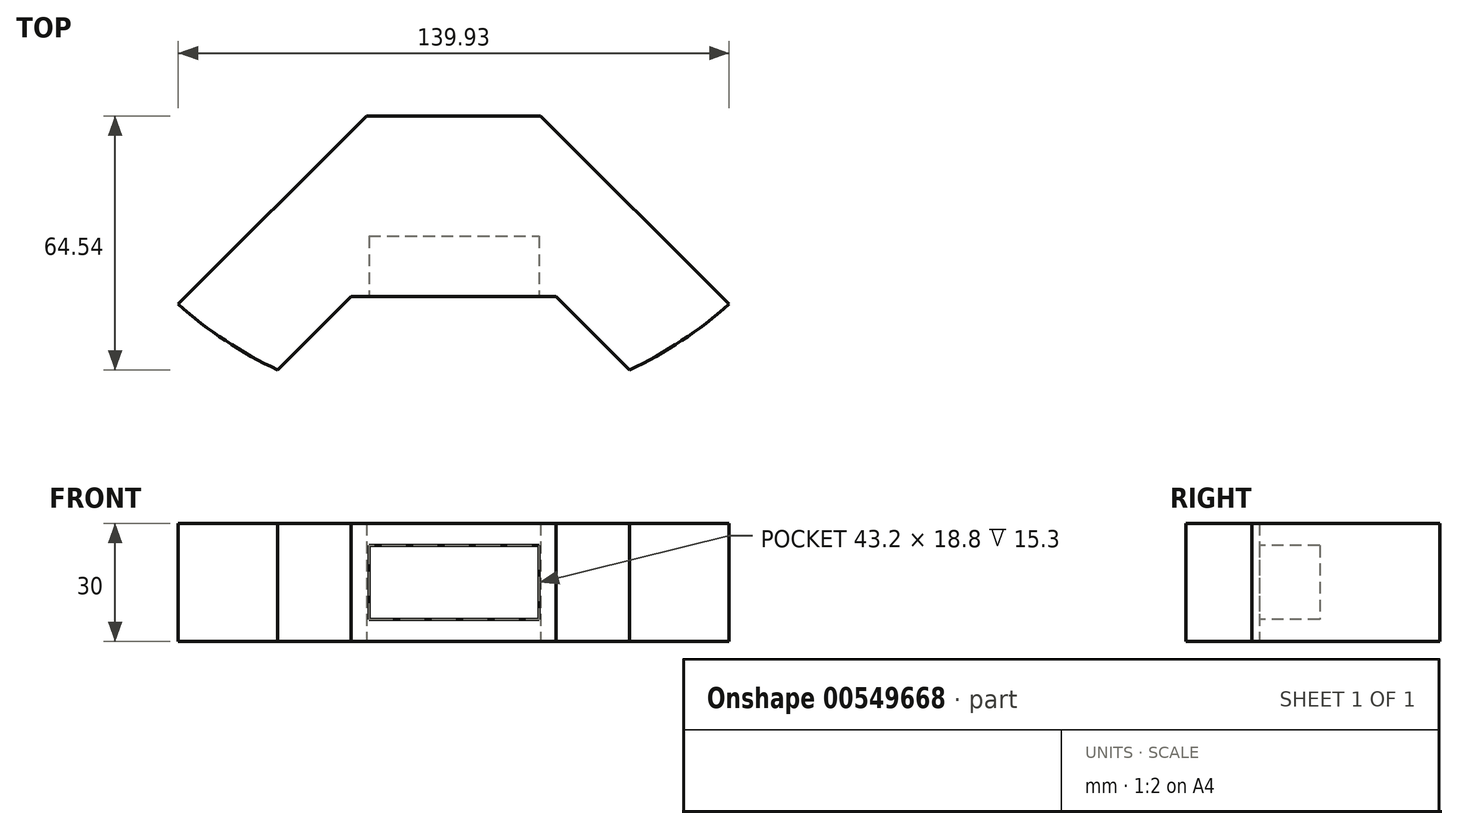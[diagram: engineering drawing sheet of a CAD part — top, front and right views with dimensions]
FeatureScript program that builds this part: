
annotation { "Feature Type Name" : "Feature", "Feature Type Description" : "" }
export const myFeature = defineFeature(function(context is Context, id is Id, definition is map)
    precondition{}
    {
        {
            var Q0;
            Q0=qCreatedBy(makeId("Top.planeOp"),FACE);
            var sketch = newSketch(context, id + "F0", { "sketchPlane" : qUnion([Q0])});
            skCircle(sketch, "E0", {"center": v(-0.1, 1.02) * mm, "radius": 105 * mm});
            skLineSegment(sketch, "E1", {"start": v(-0.1, 106.02) * mm, "end": v(-0.1, -103.98) * mm});
            skLineSegment(sketch, "E2", {"start": v(-0.1, 1.02) * mm, "end": v(-74.34, -73.22) * mm});
            skLineSegment(sketch, "E3", {"start": v(-0.1, 1.02) * mm, "end": v(74.15, -73.22) * mm});
            skLineSegment(sketch, "E4", {"start": v(-0.1, 1.02) * mm, "end": v(-0.1, 106.02) * mm});
            skLineSegment(sketch, "E5", {"start": v(-0.1, -49.26) * mm, "end": v(-44.81, -93.98) * mm});
            skLineSegment(sketch, "E6", {"start": v(-0.1, -49.26) * mm, "end": v(44.63, -93.98) * mm});
            skLineSegment(sketch, "E7", {"start": v(-18.48, 104.81) * mm, "end": v(-0.08, 104.81) * mm});
            skLineSegment(sketch, "E8.bottom", {"start": v(-18.48, 104.81) * mm, "end": v(18.7, 104.81) * mm});
            skLineSegment(sketch, "E8.top", {"start": v(-18.48, 26.11) * mm, "end": v(18.7, 26.11) * mm});
            skLineSegment(sketch, "E8.left", {"start": v(-18.48, 104.81) * mm, "end": v(-18.48, 26.11) * mm});
            skLineSegment(sketch, "E8.right", {"start": v(18.7, 104.81) * mm, "end": v(18.7, 26.11) * mm});
            skLineSegment(sketch, "E9.bottom", {"start": v(-39.87, 13.1) * mm, "end": v(-13.5, -13.1) * mm});
            skLineSegment(sketch, "E9.top", {"start": v(-95.34, -42.72) * mm, "end": v(-68.97, -68.93) * mm});
            skLineSegment(sketch, "E9.left", {"start": v(-39.87, 13.1) * mm, "end": v(-95.34, -42.72) * mm});
            skLineSegment(sketch, "E9.right", {"start": v(-13.5, -13.1) * mm, "end": v(-68.97, -68.93) * mm});
            skLineSegment(sketch, "E10.bottom", {"start": v(14.2, -12.89) * mm, "end": v(40.59, 13.3) * mm});
            skLineSegment(sketch, "E10.top", {"start": v(69.66, -68.73) * mm, "end": v(96.04, -42.54) * mm});
            skLineSegment(sketch, "E10.left", {"start": v(14.2, -12.89) * mm, "end": v(69.66, -68.73) * mm});
            skLineSegment(sketch, "E10.right", {"start": v(40.59, 13.3) * mm, "end": v(96.04, -42.54) * mm});
            skLineSegment(sketch, "E11.bottom", {"start": v(-53.06, 61.6) * mm, "end": v(-40.34, 61.6) * mm});
            skLineSegment(sketch, "E11.top", {"start": v(-53.06, 42.87) * mm, "end": v(-40.34, 42.87) * mm});
            skLineSegment(sketch, "E11.left", {"start": v(-56.06, 58.6) * mm, "end": v(-56.06, 45.87) * mm});
            skLineSegment(sketch, "E11.right", {"start": v(-37.34, 58.6) * mm, "end": v(-37.34, 45.87) * mm});
            skLineSegment(sketch, "E12.bottom", {"start": v(40.5, 60.9) * mm, "end": v(53.23, 60.9) * mm});
            skLineSegment(sketch, "E12.top", {"start": v(40.5, 42.17) * mm, "end": v(53.23, 42.17) * mm});
            skLineSegment(sketch, "E12.left", {"start": v(37.5, 57.9) * mm, "end": v(37.5, 45.17) * mm});
            skLineSegment(sketch, "E12.right", {"start": v(56.23, 57.9) * mm, "end": v(56.23, 45.17) * mm});
            skCircle(sketch, "E13", {"center": v(-29.4, 90.6) * mm, "radius": 6.5 * mm});
            skCircle(sketch, "E14", {"center": v(29.62, 90.6) * mm, "radius": 6.5 * mm});
            skCircle(sketch, "E15", {"center": v(-90.99, -22.64) * mm, "radius": 6.5 * mm});
            skCircle(sketch, "E16", {"center": v(91.64, -22.64) * mm, "radius": 6.5 * mm});
            skPoint(sketch, "E17.visualSharp", {"position": v(-56.06, 61.6) * mm});
            skArc(sketch, "E17.filletArc", {"start": v(-53.06, 61.6) * mm, "mid": v(-55.19, 60.72) * mm, "end": v(-56.06, 58.6) * mm});
            skPoint(sketch, "E18.visualSharp", {"position": v(-37.34, 61.6) * mm});
            skArc(sketch, "E18.filletArc", {"start": v(-37.34, 58.6) * mm, "mid": v(-38.22, 60.72) * mm, "end": v(-40.34, 61.6) * mm});
            skPoint(sketch, "E19.visualSharp", {"position": v(-37.34, 42.87) * mm});
            skArc(sketch, "E19.filletArc", {"start": v(-40.34, 42.87) * mm, "mid": v(-38.22, 43.75) * mm, "end": v(-37.34, 45.87) * mm});
            skPoint(sketch, "E20.visualSharp", {"position": v(-56.06, 42.87) * mm});
            skArc(sketch, "E20.filletArc", {"start": v(-56.06, 45.87) * mm, "mid": v(-55.19, 43.75) * mm, "end": v(-53.06, 42.87) * mm});
            skPoint(sketch, "E21.visualSharp", {"position": v(37.5, 60.9) * mm});
            skArc(sketch, "E21.filletArc", {"start": v(40.5, 60.9) * mm, "mid": v(38.39, 60.01) * mm, "end": v(37.5, 57.9) * mm});
            skPoint(sketch, "E22.visualSharp", {"position": v(56.23, 60.9) * mm});
            skArc(sketch, "E22.filletArc", {"start": v(56.23, 57.9) * mm, "mid": v(55.35, 60.01) * mm, "end": v(53.23, 60.9) * mm});
            skPoint(sketch, "E23.visualSharp", {"position": v(56.23, 42.17) * mm});
            skArc(sketch, "E23.filletArc", {"start": v(53.23, 42.17) * mm, "mid": v(55.35, 43.05) * mm, "end": v(56.23, 45.17) * mm});
            skPoint(sketch, "E24.visualSharp", {"position": v(37.5, 42.17) * mm});
            skArc(sketch, "E24.filletArc", {"start": v(37.5, 45.17) * mm, "mid": v(38.39, 43.05) * mm, "end": v(40.5, 42.17) * mm});
            skLineSegment(sketch, "E25", {"start": v(-26.13, -75.3) * mm, "end": v(25.94, -75.3) * mm});
            skLineSegment(sketch, "E26", {"start": v(-0.1, -7.3) * mm, "end": v(-70.06, -77.27) * mm});
            skLineSegment(sketch, "E27", {"start": v(-0.1, -7.3) * mm, "end": v(69.87, -77.27) * mm});
            skLineSegment(sketch, "E28", {"start": v(-22.23, -29.44) * mm, "end": v(22.04, -29.44) * mm});
            skSolve(sketch);
        }
        {
            var Q0;
            {var subQ0=sQuery(id+"F0.wireOp",EDGE,"E6");var subQ1=sQuery(id+"F0.wireOp",EDGE,"E0");var subQ2=makeQuery(id+"F0.imprint","INTERSECT",VERTEX,{"derivedFrom":[subQ1,subQ0]});Q0=makeQuery(id+"F0.imprint","IMPRINT",FACE,{"disambiguationData":[TD([[makeQuery(id+"F0.imprint","IMPRINT",EDGE,{"disambiguationData":[TD([[subQ2,-1.0]])],"derivedFrom":subQ1}),1.0]])]});}
            var Q1;
            {var subQ0=sQuery(id+"F0.wireOp",EDGE,"E5");var subQ1=sQuery(id+"F0.wireOp",EDGE,"E0");var subQ2=makeQuery(id+"F0.imprint","INTERSECT",VERTEX,{"derivedFrom":[subQ1,subQ0]});Q1=makeQuery(id+"F0.imprint","IMPRINT",FACE,{"disambiguationData":[TD([[makeQuery(id+"F0.imprint","IMPRINT",EDGE,{"disambiguationData":[TD([[subQ2,1.0]])],"derivedFrom":subQ1}),1.0]])]});}
            var Q2;
            {var subQ0=sQuery(id+"F0.wireOp",EDGE,"E5");var subQ3=sQuery(id+"F0.wireOp",EDGE,"E25");var subQ5=makeQuery(id+"F0.imprint","INTERSECT",VERTEX,{"derivedFrom":[subQ0,subQ3]});Q2=makeQuery(id+"F0.imprint","IMPRINT",FACE,{"disambiguationData":[TD([[makeQuery(id+"F0.imprint","IMPRINT",EDGE,{"disambiguationData":[TD([[subQ5,-1.0]])],"derivedFrom":subQ3}),1.0]])]});}
            var Q3;
            {var subQ0=sQuery(id+"F0.wireOp",EDGE,"E6");var subQ3=sQuery(id+"F0.wireOp",EDGE,"E25");var subQ5=makeQuery(id+"F0.imprint","INTERSECT",VERTEX,{"derivedFrom":[subQ0,subQ3]});Q3=makeQuery(id+"F0.imprint","IMPRINT",FACE,{"disambiguationData":[TD([[makeQuery(id+"F0.imprint","IMPRINT",EDGE,{"disambiguationData":[TD([[subQ5,1.0]])],"derivedFrom":subQ3}),1.0]])]});}
            extrude(context, id + "F1", {"entities" : qUnion([Q0, Q1, Q2, Q3]), "depth" : 30 * mm, "offsetDistance" : 25.4 * mm});
        }
        {
            var Q0;
            Q0=makeQuery(id+"F1.opExtrude","SWEPT_FACE",FACE,{"disambiguationData":[OSD([sQuery(id+"F0.wireOp",EDGE,"E25")])]});
            var sketch = newSketch(context, id + "F2", { "sketchPlane" : qUnion([Q0])});
            skLineSegment(sketch, "E29.bottom", {"start": v(-21.6, 24.4) * mm, "end": v(21.6, 24.4) * mm});
            skLineSegment(sketch, "E29.top", {"start": v(-21.6, 5.6) * mm, "end": v(21.6, 5.6) * mm});
            skLineSegment(sketch, "E29.left", {"start": v(-21.6, 24.4) * mm, "end": v(-21.6, 5.6) * mm});
            skLineSegment(sketch, "E29.right", {"start": v(21.6, 24.4) * mm, "end": v(21.6, 5.6) * mm});
            skPoint(sketch, "E29.middle", {"position": v(0, 15) * mm});
            skSolve(sketch);
        }
        {
            var Q0;
            Q0=makeQuery(id+"F2.imprint","IMPRINT",FACE,{"disambiguationData":[TD([[makeQuery(id+"F2.imprint","IMPRINT",EDGE,{"derivedFrom":sQuery(id+"F2.wireOp",EDGE,"E29.bottom")}),-1.0]])]});
            extrude(context, id + "F3", {"entities" : qUnion([Q0]), "operationType" : NewBodyOperationType.REMOVE, "oppositeDirection" : true, "depth" : 15.3 * mm, "offsetDistance" : 25.4 * mm});
        }
    });
